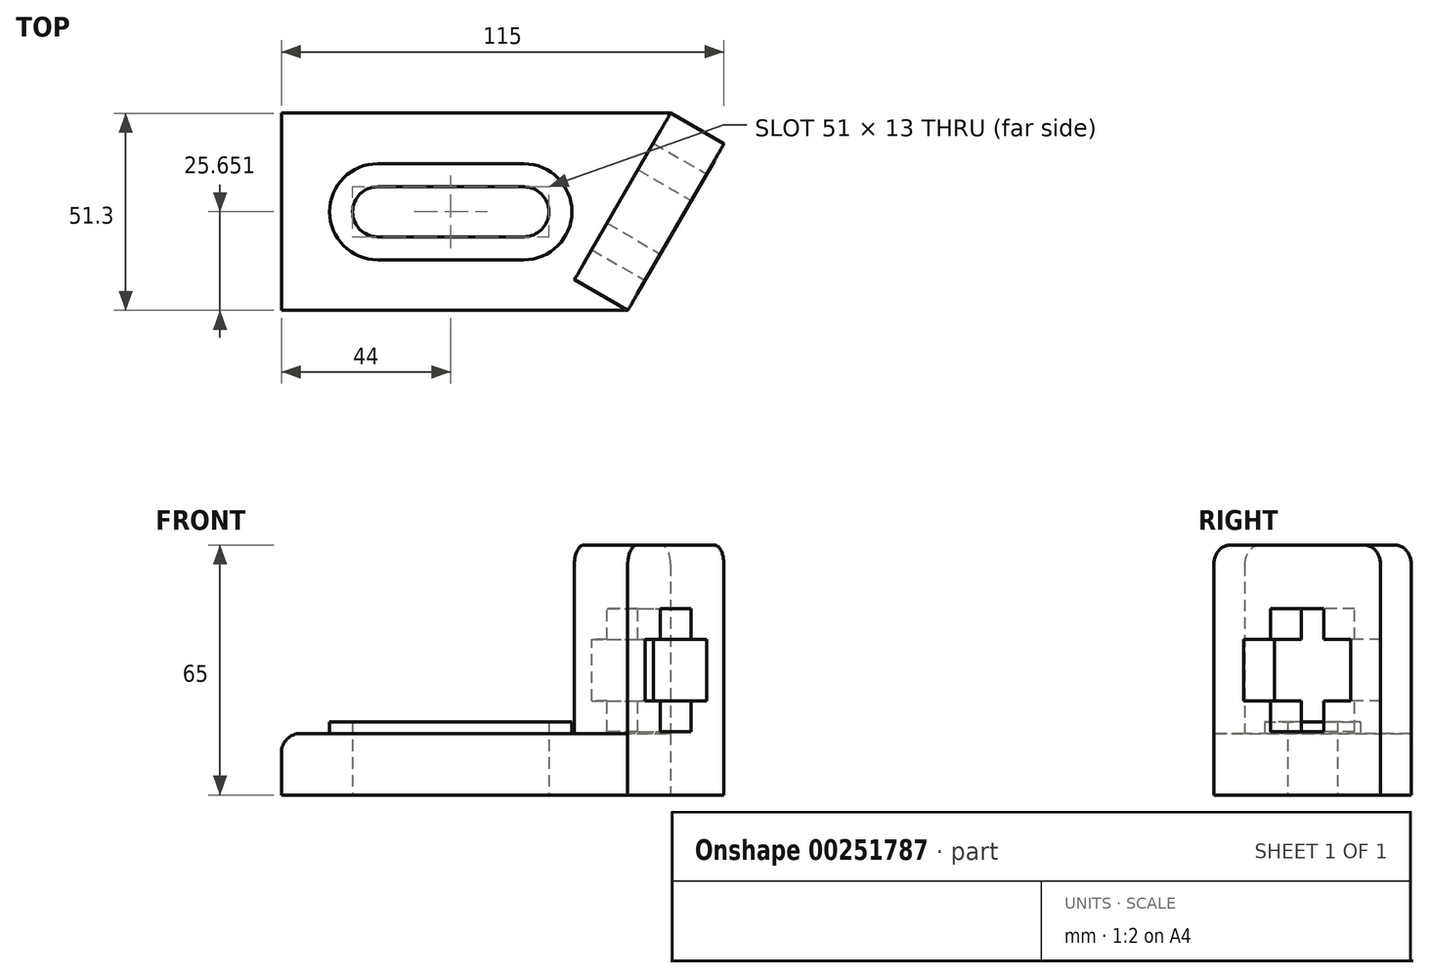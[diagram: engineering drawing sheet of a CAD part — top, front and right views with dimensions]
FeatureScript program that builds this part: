
annotation { "Feature Type Name" : "Feature", "Feature Type Description" : "" }
export const myFeature = defineFeature(function(context is Context, id is Id, definition is map)
    precondition{}
    {
        {
            var Q0;
            Q0=qCreatedBy(makeId("Top.planeOp"),FACE);
            var sketch = newSketch(context, id + "F0", { "sketchPlane" : qUnion([Q0])});
            skLineSegment(sketch, "E0", {"start": v(0, 0) * mm, "end": v(25, 43.3) * mm});
            skLineSegment(sketch, "E1", {"start": v(25, 43.3) * mm, "end": v(11.14, 51.3) * mm});
            skLineSegment(sketch, "E2", {"start": v(11.14, 51.3) * mm, "end": v(-13.86, 8) * mm});
            skLineSegment(sketch, "E3", {"start": v(-13.86, 8) * mm, "end": v(0, 0) * mm});
            skSolve(sketch);
        }
        {
            var Q0;
            Q0 = qSketchRegion(id + "F0", true);
            extrude(context, id + "F1", {"entities" : qUnion([Q0]), "endBound" : BoundingType.SYMMETRIC, "depth" : 65 * mm});
        }
        {
            var Q0;
            Q0=qCreatedBy(makeId("Top.planeOp"),FACE);
            var sketch = newSketch(context, id + "F2", { "sketchPlane" : qUnion([Q0])});
            skLineSegment(sketch, "E4", {"start": v(0, 0) * mm, "end": v(-90, 0) * mm});
            skLineSegment(sketch, "E5", {"start": v(-90, 0) * mm, "end": v(-90, 51.3) * mm});
            skLineSegment(sketch, "E6", {"start": v(-90, 51.3) * mm, "end": v(11.14, 51.3) * mm});
            skSolve(sketch);
        }
        {
            var Q0;
            Q0=makeQuery(id+"F1.opExtrude","CAP_FACE",FACE,{"disambiguationData":[OSD([sQuery(id+"F0.wireOp",EDGE,"E0"),sQuery(id+"F0.wireOp",EDGE,"E1"),sQuery(id+"F0.wireOp",EDGE,"E2"),sQuery(id+"F0.wireOp",EDGE,"E3")])],"isStart":true});
            var sketch = newSketch(context, id + "F3", { "sketchPlane" : qUnion([Q0])});
            skLineSegment(sketch, "E7.0", {"start": v(0, 0) * mm, "end": v(-90, 0) * mm});
            skLineSegment(sketch, "E8.0", {"start": v(-90, 0) * mm, "end": v(-90, -51.3) * mm});
            skLineSegment(sketch, "E9.0", {"start": v(-90, -51.3) * mm, "end": v(11.14, -51.3) * mm});
            skLineSegment(sketch, "E10.0", {"start": v(11.14, -51.3) * mm, "end": v(-13.86, -8) * mm});
            skPoint(sketch, "E11.0", {"position": v(-6.93, -4) * mm});
            skSolve(sketch);
        }
        {
            var Q0;
            Q0=makeQuery(id+"F3.imprint","IMPRINT",FACE,{"disambiguationData":[TD([[makeQuery(id+"F3.imprint","IMPRINT",EDGE,{"derivedFrom":sQuery(id+"F3.wireOp",EDGE,"E10.0")}),-1.0]])]});
            var sketch = newSketch(context, id + "F4", { "sketchPlane" : qUnion([Q0])});
            skLineSegment(sketch, "E12.0", {"start": v(0, 0) * mm, "end": v(-90, 0) * mm});
            skLineSegment(sketch, "E13.0", {"start": v(-13.86, -8) * mm, "end": v(0, 0) * mm});
            skLineSegment(sketch, "E14.0", {"start": v(11.14, -51.3) * mm, "end": v(-13.86, -8) * mm});
            skLineSegment(sketch, "E15.0", {"start": v(-90, -51.3) * mm, "end": v(11.14, -51.3) * mm});
            skLineSegment(sketch, "E16.0", {"start": v(-90, 0) * mm, "end": v(-90, -51.3) * mm});
            skSolve(sketch);
        }
        {
            var Q0;
            Q0 = qSketchRegion(id + "F4", true);
            extrude(context, id + "F5", {"entities" : qUnion([Q0]), "operationType" : NewBodyOperationType.ADD, "oppositeDirection" : true, "depth" : 16 * mm});
        }
        {
            var Q0;
            Q0=makeQuery(id+"F1.opExtrude","CAP_EDGE",EDGE,{"disambiguationData":[OSD([sQuery(id+"F0.wireOp",EDGE,"E3")])],"isStart":false});
            var Q1;
            Q1=makeQuery(id+"F1.opExtrude","CAP_EDGE",EDGE,{"disambiguationData":[OSD([sQuery(id+"F0.wireOp",EDGE,"E1")])],"isStart":false});
            fillet(context, id + "F6", {"entities" : qUnion([Q0, Q1]), "radius" : 5 * mm, "tangentPropagation" : true, "allowEdgeOverflow" : false});
        }
        {
            var Q0;
            Q0=makeQuery(id+"F5.opExtrude","CAP_FACE",FACE,{"disambiguationData":[OSD([sQuery(id+"F4.wireOp",EDGE,"E12.0"),sQuery(id+"F4.wireOp",EDGE,"E13.0"),sQuery(id+"F4.wireOp",EDGE,"E14.0"),sQuery(id+"F4.wireOp",EDGE,"E15.0"),sQuery(id+"F4.wireOp",EDGE,"E16.0")])],"isStart":false});
            var sketch = newSketch(context, id + "F7", { "sketchPlane" : qUnion([Q0])});
            skLineSegment(sketch, "E17.bottom", {"start": v(-27, 13.15) * mm, "end": v(-65, 13.15) * mm});
            skLineSegment(sketch, "E17.top", {"start": v(-27, 38.15) * mm, "end": v(-65, 38.15) * mm});
            skLineSegment(sketch, "E17.left", {"start": v(-27, 13.15) * mm, "end": v(-27, 38.15) * mm});
            skLineSegment(sketch, "E17.right", {"start": v(-65, 13.15) * mm, "end": v(-65, 38.15) * mm});
            skPoint(sketch, "E17.middle", {"position": v(-46, 25.65) * mm});
            skPoint(sketch, "E17.middle.positionSnap0", {"position": v(-90, 25.65) * mm});
            skPoint(sketch, "E17.centerSnap0", {"position": v(-90, 25.65) * mm});
            skLineSegment(sketch, "E18.bottom", {"start": v(-27, 19.15) * mm, "end": v(-65, 19.15) * mm});
            skLineSegment(sketch, "E18.top", {"start": v(-27, 32.15) * mm, "end": v(-65, 32.15) * mm});
            skLineSegment(sketch, "E18.left", {"start": v(-27, 19.15) * mm, "end": v(-27, 32.15) * mm});
            skLineSegment(sketch, "E18.right", {"start": v(-65, 19.15) * mm, "end": v(-65, 32.15) * mm});
            skCircle(sketch, "E19", {"center": v(-65, 25.65) * mm, "radius": 12.5 * mm});
            skCircle(sketch, "E20", {"center": v(-65, 25.65) * mm, "radius": 6.5 * mm});
            skCircle(sketch, "E21", {"center": v(-27, 25.65) * mm, "radius": 6.5 * mm});
            skCircle(sketch, "E22", {"center": v(-27, 25.65) * mm, "radius": 12.5 * mm});
            skSolve(sketch);
        }
        {
            var Q0;
            {var subQ0=sQuery(id+"F7.wireOp",EDGE,"E19");var subQ1=sQuery(id+"F7.wireOp",EDGE,"E17.right");var subQ2=makeQuery(id+"F7.imprint","INTERSECT",VERTEX,{"derivedFrom":[sQuery(id+"F7.wireOp",EDGE,"E17.bottom"),subQ1,subQ0]});Q0=makeQuery(id+"F7.imprint","IMPRINT",FACE,{"disambiguationData":[TD([[makeQuery(id+"F7.imprint","IMPRINT",EDGE,{"disambiguationData":[TD([[subQ2,1.0]])],"derivedFrom":subQ0}),1.0]])]});}
            var Q1;
            {var subQ0=sQuery(id+"F7.wireOp",EDGE,"E19");var subQ3=sQuery(id+"F7.wireOp",EDGE,"E18.bottom");var subQ5=makeQuery(id+"F7.imprint","INTERSECT",VERTEX,{"derivedFrom":[subQ3,subQ0]});Q1=makeQuery(id+"F7.imprint","IMPRINT",FACE,{"disambiguationData":[TD([[makeQuery(id+"F7.imprint","IMPRINT",EDGE,{"disambiguationData":[TD([[subQ5,1.0]])],"derivedFrom":subQ0}),1.0]])]});}
            var Q2;
            {var subQ0=sQuery(id+"F7.wireOp",EDGE,"E17.bottom");Q2=makeQuery(id+"F7.imprint","IMPRINT",FACE,{"disambiguationData":[TD([[makeQuery(id+"F7.imprint","IMPRINT",EDGE,{"derivedFrom":subQ0}),-1.0]])]});}
            var Q3;
            {var subQ0=sQuery(id+"F7.wireOp",EDGE,"E22");var subQ1=sQuery(id+"F7.wireOp",EDGE,"E17.left");var subQ2=makeQuery(id+"F7.imprint","INTERSECT",VERTEX,{"derivedFrom":[sQuery(id+"F7.wireOp",EDGE,"E17.bottom"),subQ1,subQ0]});Q3=makeQuery(id+"F7.imprint","IMPRINT",FACE,{"disambiguationData":[TD([[makeQuery(id+"F7.imprint","IMPRINT",EDGE,{"disambiguationData":[TD([[subQ2,-1.0]])],"derivedFrom":subQ0}),1.0]])]});}
            var Q4;
            {var subQ0=sQuery(id+"F7.wireOp",EDGE,"E22");var subQ3=sQuery(id+"F7.wireOp",EDGE,"E18.bottom");var subQ5=makeQuery(id+"F7.imprint","INTERSECT",VERTEX,{"derivedFrom":[subQ3,subQ0]});Q4=makeQuery(id+"F7.imprint","IMPRINT",FACE,{"disambiguationData":[TD([[makeQuery(id+"F7.imprint","IMPRINT",EDGE,{"disambiguationData":[TD([[subQ5,-1.0]])],"derivedFrom":subQ0}),1.0]])]});}
            var Q5;
            {var subQ0=sQuery(id+"F7.wireOp",EDGE,"E22");var subQ3=sQuery(id+"F7.wireOp",EDGE,"E18.top");var subQ5=makeQuery(id+"F7.imprint","INTERSECT",VERTEX,{"derivedFrom":[subQ3,subQ0]});Q5=makeQuery(id+"F7.imprint","IMPRINT",FACE,{"disambiguationData":[TD([[makeQuery(id+"F7.imprint","IMPRINT",EDGE,{"disambiguationData":[TD([[subQ5,1.0]])],"derivedFrom":subQ0}),1.0]])]});}
            var Q6;
            {var subQ0=sQuery(id+"F7.wireOp",EDGE,"E19");var subQ3=sQuery(id+"F7.wireOp",EDGE,"E18.top");var subQ5=makeQuery(id+"F7.imprint","INTERSECT",VERTEX,{"derivedFrom":[subQ3,subQ0]});Q6=makeQuery(id+"F7.imprint","IMPRINT",FACE,{"disambiguationData":[TD([[makeQuery(id+"F7.imprint","IMPRINT",EDGE,{"disambiguationData":[TD([[subQ5,-1.0]])],"derivedFrom":subQ0}),1.0]])]});}
            var Q7;
            {var subQ0=sQuery(id+"F7.wireOp",EDGE,"E17.top");Q7=makeQuery(id+"F7.imprint","IMPRINT",FACE,{"disambiguationData":[TD([[makeQuery(id+"F7.imprint","IMPRINT",EDGE,{"derivedFrom":subQ0}),1.0]])]});}
            extrude(context, id + "F8", {"entities" : qUnion([Q0, Q1, Q2, Q3, Q4, Q5, Q6, Q7]), "operationType" : NewBodyOperationType.ADD, "depth" : 3 * mm});
        }
        {
            var Q0;
            Q0=makeQuery(id+"F8.boolean.opBoolean","SPLIT",FACE,{"disambiguationData":[TD([makeQuery(id+"F8.opExtrude","SWEPT_FACE",FACE,{"disambiguationData":[OSD([sQuery(id+"F7.wireOp",EDGE,"E18.bottom")])]})])],"derivedFrom":makeQuery(id+"F5.opExtrude","CAP_FACE",FACE,{"disambiguationData":[OSD([sQuery(id+"F4.wireOp",EDGE,"E12.0"),sQuery(id+"F4.wireOp",EDGE,"E13.0"),sQuery(id+"F4.wireOp",EDGE,"E14.0"),sQuery(id+"F4.wireOp",EDGE,"E15.0"),sQuery(id+"F4.wireOp",EDGE,"E16.0")])],"isStart":false})});
            extrude(context, id + "F9", {"entities" : qUnion([Q0]), "operationType" : NewBodyOperationType.REMOVE, "endBound" : BoundingType.THROUGH_ALL, "oppositeDirection" : true, "depth" : 25 * mm});
        }
        {
            var Q0;
            Q0=makeQuery(id+"F1.opExtrude","SWEPT_FACE",FACE,{"disambiguationData":[OSD([sQuery(id+"F0.wireOp",EDGE,"E0")])]});
            var sketch = newSketch(context, id + "F10", { "sketchPlane" : qUnion([Q0])});
            skLineSegment(sketch, "E23.bottom", {"start": v(41, -8) * mm, "end": v(33, -8) * mm});
            skLineSegment(sketch, "E23.top", {"start": v(41, 8) * mm, "end": v(33, 8) * mm});
            skLineSegment(sketch, "E23.left", {"start": v(41, -8) * mm, "end": v(41, 8) * mm});
            skLineSegment(sketch, "E23.right", {"start": v(9, -8) * mm, "end": v(9, 8) * mm});
            skPoint(sketch, "E23.middle", {"position": v(25, 0) * mm});
            skLineSegment(sketch, "E24.bottom", {"start": v(33, -16) * mm, "end": v(17, -16) * mm});
            skLineSegment(sketch, "E24.top", {"start": v(33, 16) * mm, "end": v(17, 16) * mm});
            skLineSegment(sketch, "E24.left", {"start": v(33, -16) * mm, "end": v(33, -8) * mm});
            skLineSegment(sketch, "E24.right", {"start": v(17, -16) * mm, "end": v(17, -8) * mm});
            skLineSegment(sketch, "E25.trimOffspring", {"start": v(17, 8) * mm, "end": v(9, 8) * mm});
            skLineSegment(sketch, "E26.trimOffspring", {"start": v(17, 8) * mm, "end": v(17, 16) * mm});
            skLineSegment(sketch, "E27.trimOffspring", {"start": v(33, 8) * mm, "end": v(33, 16) * mm});
            skLineSegment(sketch, "E28.trimOffspring", {"start": v(17, -8) * mm, "end": v(9, -8) * mm});
            skSolve(sketch);
        }
        {
            var Q0;
            Q0 = qSketchRegion(id + "F10", true);
            extrude(context, id + "F11", {"entities" : qUnion([Q0]), "operationType" : NewBodyOperationType.REMOVE, "oppositeDirection" : true, "depth" : 20 * mm});
        }
        {
            var Q0;
            Q0=makeQuery(id+"F5.opExtrude","CAP_EDGE",EDGE,{"disambiguationData":[OSD([sQuery(id+"F4.wireOp",EDGE,"E16.0")])],"isStart":false});
            fillet(context, id + "F12", {"entities" : qUnion([Q0]), "radius" : 5 * mm, "tangentPropagation" : true, "allowEdgeOverflow" : false});
        }
    });
